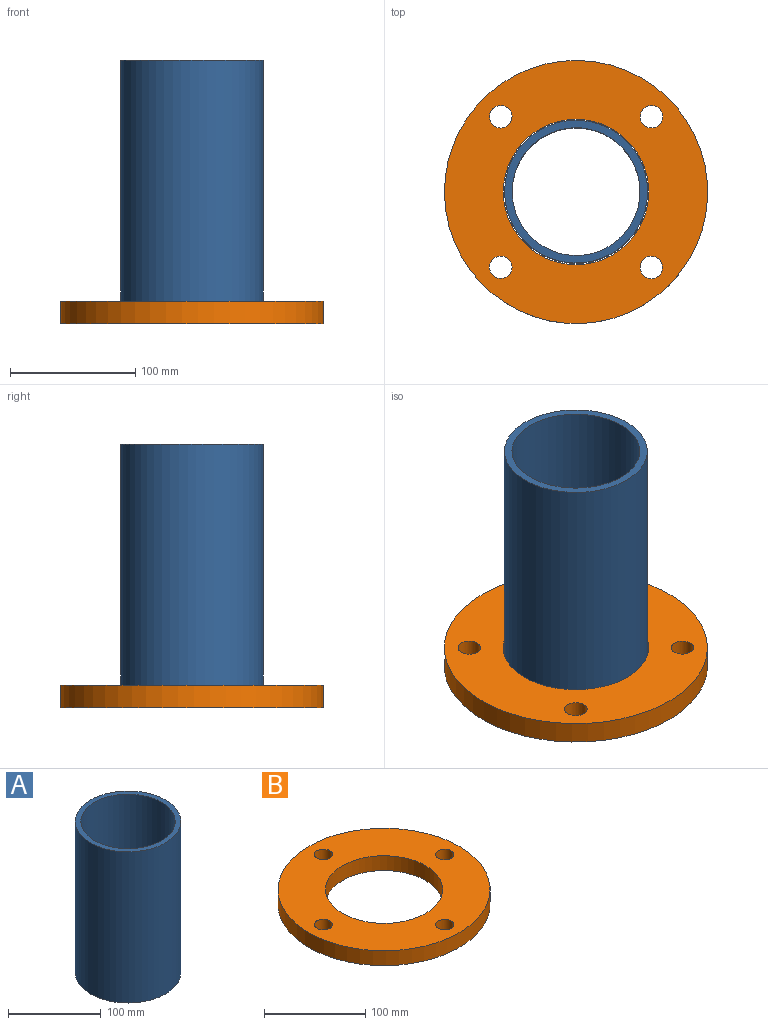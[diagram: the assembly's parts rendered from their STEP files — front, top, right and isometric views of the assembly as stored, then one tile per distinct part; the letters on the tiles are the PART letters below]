
ASSEMBLY  parts=2 mates=1
PART A: 4 faces, bbox 114x114x200 mm
  f0: cylinder r=51mm len=200mm, axis (0,0,-1), area 64088.5mm2, adj f2,f3
  f1: cylinder r=57mm len=200mm, axis (0,0,-1), area 71628.3mm2, adj f2,f3
  f2: plane 114x114mm, normal (0,0,1), area 2035.8mm2, adj f0,f1
  f3: plane 114x114mm, normal (0,0,-1), area 2035.8mm2, adj f0,f1
PART B: 8 faces, bbox 210x210x18 mm
  f0: cylinder r=9mm len=18mm, axis (0,0,-1), area 1017.9mm2, adj f6,f7
  f1: cylinder r=9mm len=18mm, axis (0,0,-1), area 1017.9mm2, adj f6,f7
  f2: cylinder r=9mm len=18mm, axis (0,0,-1), area 1017.9mm2, adj f6,f7
  f3: cylinder r=9mm len=18mm, axis (0,0,-1), area 1017.9mm2, adj f6,f7
  f4: cylinder r=58mm len=116mm, axis (0,0,-1), area 6559.6mm2, adj f6,f7
  f5: cylinder r=105mm len=210mm, axis (0,0,-1), area 11875.2mm2, adj f6,f7
  f6: plane 210x210mm, normal (0,0,1), area 23049.9mm2, adj f0,f1,f2,f3,f4,f5
  f7: plane 210x210mm, normal (0,0,-1), area 23049.9mm2, adj f0,f1,f2,f3,f4,f5
PLACE A t=(-2108.57,195.95,-75.79)mm
PLACE B rot(axis=(0,0,-1),45deg) t=(-1867.87,2375.25,-85.79)mm
MATE fastened B.f4 <-> A.f0  axis (0,0,1) through (311.43,195.95,-75.79)mm
